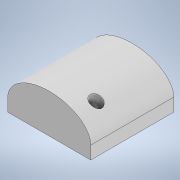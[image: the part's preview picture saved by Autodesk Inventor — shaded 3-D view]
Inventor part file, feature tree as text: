
AUTODESK INVENTOR PART (.ipt)
format: ipt  version: 2021 (Build 250183000, 183)  size: 238,592 bytes
history: native  units: mm
features: sketch x12, extrude x10, plane x2, other x1, shell x1, hole x1, thread x1
ambient origin geometry x8: Origin, YZ Plane, XZ Plane, XY Plane, X Axis, Y Axis, Z Axis, Center Point
bodies: Body1 (feature_tree)
feature tree (28):
  other  "Sólido1"
  sketch  "Boceto1"  dims[d0=2.5mm d2=3.0mm d3=4.0mm]
  extrude  "Extrusión1"  Depth=3.0mm
  shell  "Vaciado1"  Thickness=4.0mm
  plane  "Plano de trabajo2"
  extrude  "Extrusión2"  Depth=2.0mm
  extrude  "Extrusión3"  Depth=64.0mm
  sketch  "Boceto11"  dims[d25=30.0mm d26=0.0mm d27=0.25mm d28=45.0deg]
  sketch  "Boceto12"  dims[d29=2.0mm d30=1.0mm]
  extrude  "Extrusión9"  Depth=20.0mm TaperAngle=0.0deg
  extrude  "Extrusión10"  Depth=2.0mm TaperAngle=0.0deg
  extrude  "Extrusión4"  Depth=10.0mm
  hole  "Agujero1"  [1 undecoded]
  plane  "Plano de trabajo3"
  extrude  "Extrusión6"  Depth=8.0mm
  extrude  "Extrusión8"  Depth=0.25mm
  thread  "Rosca1"  [1 undecoded]
  extrude  "Extrusión13"  Depth=1.0mm
  extrude  "Extrusión14"  TaperAngle=45.0deg  [1 undecoded]
  sketch  "Boceto2"  dims[d4=4.0mm d6=2.0mm]
  sketch  "Boceto3"  dims[d7=30.0mm d8=64.0mm]
  sketch  "Boceto4"  dims[d9=64.0mm d10=20.0mm d11=0.0mm]
  sketch  "Boceto5"  dims[d12=2.0mm d13=20.0mm d14=0.0mm]
  sketch  "Boceto6"  dims[d19=-20.0mm d20=10.0mm]
  sketch  "Boceto8"  dims[d21=16.0mm d22=16.0mm]
  sketch  "Boceto10"  dims[d23=8.0mm d24=13.0mm]
  sketch  "Boceto15"  dims[d31=3.0mm d32=45.0deg]
  sketch  "Boceto16"  dims[d33=2.0mm d34=5.0mm d35=4.0mm d36=0.0mm d37=0.0mm d38=4.0mm d39=7.0mm d40=0.0mm d42=4.0mm d43=4.0mm d44=6.0mm d45=4.0mm d46=2.0mm d47=90.0deg d48=10.0mm d49=0.0mm d55=-3.0mm d56=50.0mm d57=9.0mm d58=0.0mm d59=0.0mm d63=4.0mm d64=2.5mm d65=4.0mm d66=5.0mm d67=0.0mm d68=0.0mm d69=10.0mm d70=10.0mm d71=0.0mm d72=0.0mm d73=64.0mm d74=0.0mm d75=20.0mm d76=20.0mm d85=2.0mm d86=0.0mm d87=13.0mm d88=1.0mm d89=0.0mm d90=13.0mm d91=9.0mm d92=2.0mm d93=0.0mm]
note: 3 required parameter values undecoded (feature->parameter linkage not recoverable at this tier; creation-order binding heuristic only, values carry confidence <= 0.55)
